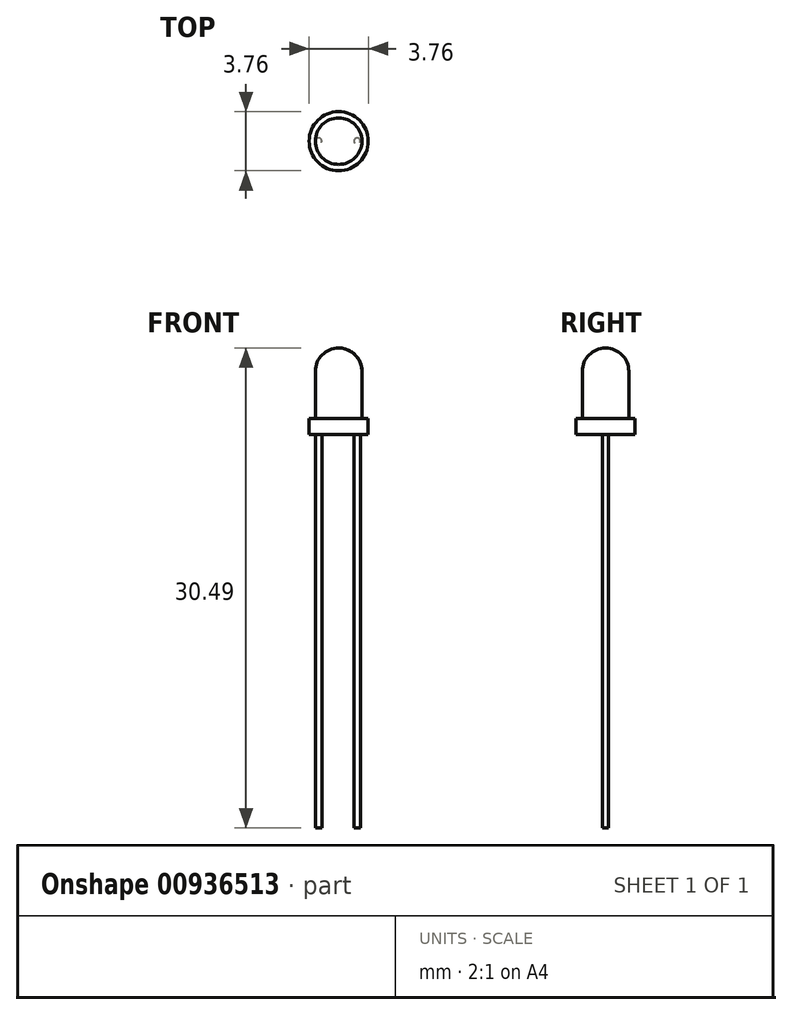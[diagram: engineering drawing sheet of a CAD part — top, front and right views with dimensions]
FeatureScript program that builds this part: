
annotation { "Feature Type Name" : "Feature", "Feature Type Description" : "" }
export const myFeature = defineFeature(function(context is Context, id is Id, definition is map)
    precondition{}
    {
        {
            var Q0;
            Q0=qCreatedBy(makeId("Front.planeOp"),FACE);
            var sketch = newSketch(context, id + "F0", { "sketchPlane" : qUnion([Q0])});
            skArc(sketch, "E0", {"start": v(0, 5.34) * mm, "mid": v(-1.04, 4.9) * mm, "end": v(-1.48, 3.86) * mm});
            skLineSegment(sketch, "E1", {"start": v(-1.48, 3.86) * mm, "end": v(-1.48, 0.85) * mm});
            skLineSegment(sketch, "E2", {"start": v(0, 5.34) * mm, "end": v(0, -0.15) * mm});
            skLineSegment(sketch, "E3", {"start": v(-1.47, 0.85) * mm, "end": v(-1.87, 0.85) * mm});
            skLineSegment(sketch, "E4", {"start": v(-1.87, 0.85) * mm, "end": v(-1.87, -0.15) * mm});
            skLineSegment(sketch, "E5", {"start": v(-1.87, -0.15) * mm, "end": v(0, -0.15) * mm});
            skSolve(sketch);
        }
        {
            var Q0;
            Q0 = qSketchRegion(id + "F0", true);
            var Q1;
            Q1=sQuery(id+"F0.wireOp",EDGE,"E2");
            revolve(context, id + "F1", {"surfaceOperationType" : NewSurfaceOperationType.NEW, "entities" : qUnion([Q0]), "axis" : qUnion([Q1]), "revolveType" : RevolveType.FULL});
        }
        {
            var Q0;
            Q0=makeQuery(id+"F1.opRevolve","SWEPT_FACE",FACE,{"disambiguationData":[OSD([sQuery(id+"F0.wireOp",EDGE,"E5")])]});
            var sketch = newSketch(context, id + "F2", { "sketchPlane" : qUnion([Q0])});
            skCircle(sketch, "E6", {"center": v(-1.27, 0) * mm, "radius": 0.2 * mm});
            skCircle(sketch, "E7", {"center": v(1.18, 0) * mm, "radius": 0.2 * mm});
            skSolve(sketch);
        }
        {
            var Q0;
            Q0 = qSketchRegion(id + "F2", true);
            extrude(context, id + "F3", {"entities" : qUnion([Q0]), "depth" : 25 * mm, "offsetDistance" : 25 * mm});
        }
    });
